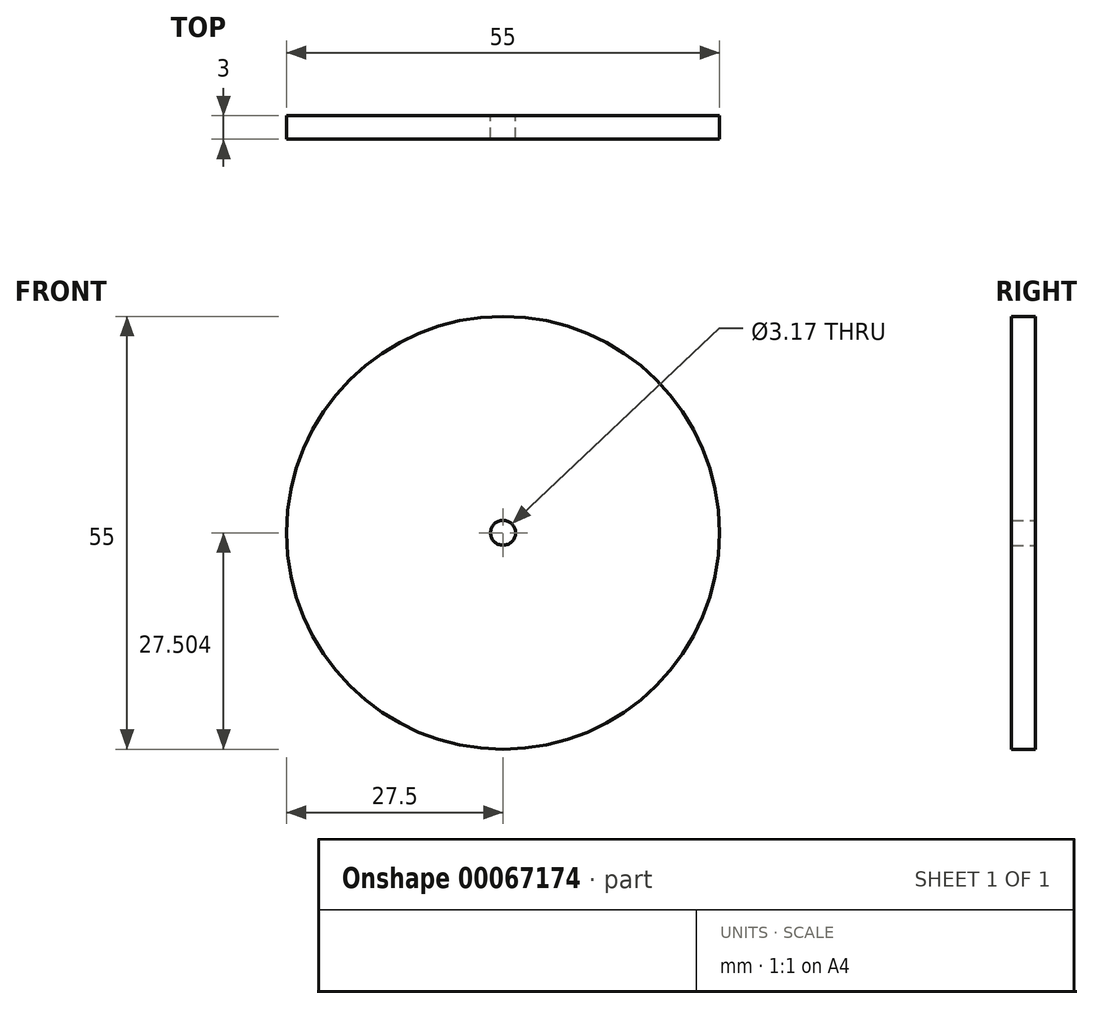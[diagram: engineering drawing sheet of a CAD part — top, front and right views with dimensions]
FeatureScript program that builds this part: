
annotation { "Feature Type Name" : "Feature", "Feature Type Description" : "" }
export const myFeature = defineFeature(function(context is Context, id is Id, definition is map)
    precondition{}
    {
        {
            var Q0;
            Q0=qCreatedBy(makeId("Front.planeOp"),FACE);
            var sketch = newSketch(context, id + "F0", { "sketchPlane" : qUnion([Q0])});
            skCircle(sketch, "E0", {"center": v(0, -1.08) * mm, "radius": 27.5 * mm});
            skCircle(sketch, "E1", {"center": v(0, -1.08) * mm, "radius": 1.59 * mm});
            skSolve(sketch);
        }
        {
            var Q0;
            Q0=makeQuery(id+"F0.imprint","IMPRINT",FACE,{"disambiguationData":[TD([[makeQuery(id+"F0.imprint","IMPRINT",EDGE,{"derivedFrom":sQuery(id+"F0.wireOp",EDGE,"E0")}),1.0]])]});
            extrude(context, id + "F1", {"entities" : qUnion([Q0]), "depth" : 3 * mm});
        }
    });
